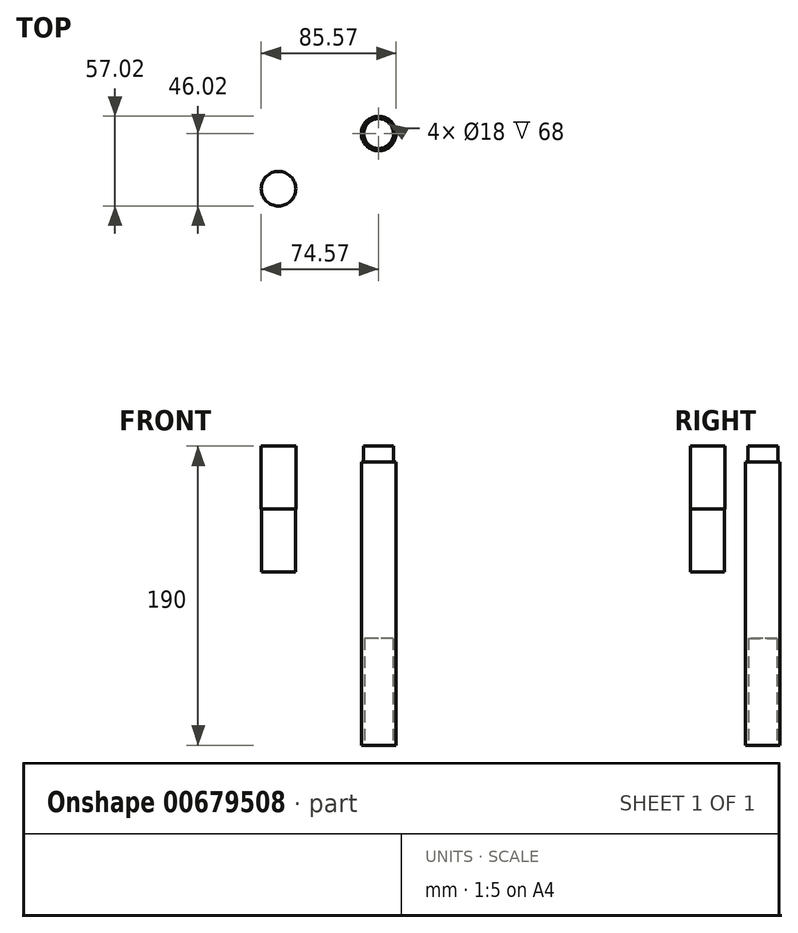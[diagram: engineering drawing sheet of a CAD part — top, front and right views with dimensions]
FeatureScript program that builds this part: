
annotation { "Feature Type Name" : "Feature", "Feature Type Description" : "" }
export const myFeature = defineFeature(function(context is Context, id is Id, definition is map)
    precondition{}
    {
        {
            var Q0;
            Q0=qCreatedBy(makeId("Top.planeOp"),FACE);
            var sketch = newSketch(context, id + "F0", { "sketchPlane" : qUnion([Q0])});
            skCircle(sketch, "E0", {"center": v(0, 0) * mm, "radius": 11 * mm});
            skSolve(sketch);
        }
        {
            var Q0;
            Q0=makeQuery(id+"F0.imprint","IMPRINT",FACE,{"disambiguationData":[TD([[makeQuery(id+"F0.imprint","IMPRINT",EDGE,{"derivedFrom":sQuery(id+"F0.wireOp",EDGE,"E0")}),1.0]])]});
            extrude(context, id + "F1", {"entities" : qUnion([Q0]), "depth" : 180 * mm, "offsetDistance" : 25 * mm});
        }
        {
            var Q0;
            Q0=makeQuery(id+"F1.opExtrude","CAP_FACE",FACE,{"disambiguationData":[OSD([sQuery(id+"F0.wireOp",EDGE,"E0")])],"isStart":false});
            var sketch = newSketch(context, id + "F2", { "sketchPlane" : qUnion([Q0])});
            skCircle(sketch, "E1", {"center": v(0, 0) * mm, "radius": 9.5 * mm});
            skSolve(sketch);
        }
        {
            var Q0;
            Q0=makeQuery(id+"F2.imprint","IMPRINT",FACE,{"disambiguationData":[TD([[makeQuery(id+"F2.imprint","IMPRINT",EDGE,{"derivedFrom":sQuery(id+"F2.wireOp",EDGE,"E1")}),1.0]])]});
            extrude(context, id + "F3", {"entities" : qUnion([Q0]), "operationType" : NewBodyOperationType.ADD, "depth" : 10 * mm, "offsetDistance" : 25 * mm});
        }
        {
            var Q0;
            Q0=makeQuery(id+"F1.opExtrude","CAP_FACE",FACE,{"disambiguationData":[OSD([sQuery(id+"F0.wireOp",EDGE,"E0")])],"isStart":true});
            var sketch = newSketch(context, id + "F4", { "sketchPlane" : qUnion([Q0])});
            skCircle(sketch, "E2", {"center": v(0, 0) * mm, "radius": 9 * mm});
            skSolve(sketch);
        }
        {
            var Q0;
            Q0 = qSketchRegion(id + "F4", true);
            extrude(context, id + "F5", {"entities" : qUnion([Q0]), "operationType" : NewBodyOperationType.REMOVE, "oppositeDirection" : true, "depth" : 68 * mm, "offsetDistance" : 25 * mm});
        }
        {
            var Q0;
            Q0=makeQuery(id+"F1.opExtrude","SWEPT_BODY",BODY,{"disambiguationData":[OSD([sQuery(id+"F0.wireOp",EDGE,"E0")])]});
            var Q1;
            Q1=makeQuery(id+"F1.opExtrude","SWEPT_FACE",FACE,{"disambiguationData":[OSD([sQuery(id+"F0.wireOp",EDGE,"E0")])]});
            circularPattern(context, id + "F6", {"entities" : qUnion([Q0]), "axis" : qUnion([Q1]), "angle" : 360 * degree, "instanceCount" : 4, "equalSpace" : true});
        }
        {
            var Q0;
            Q0=makeQuery(id+"F3.opExtrude","CAP_FACE",FACE,{"disambiguationData":[OSD([sQuery(id+"F2.wireOp",EDGE,"E1")])],"isStart":false});
            var sketch = newSketch(context, id + "F7", { "sketchPlane" : qUnion([Q0])});
            skCircle(sketch, "E3", {"center": v(-63.57, -35.02) * mm, "radius": 11 * mm});
            skSolve(sketch);
        }
        {
            var Q0;
            Q0=makeQuery(id+"F7.imprint","IMPRINT",FACE,{"disambiguationData":[TD([[makeQuery(id+"F7.imprint","IMPRINT",EDGE,{"derivedFrom":sQuery(id+"F7.wireOp",EDGE,"E3")}),1.0]])]});
            extrude(context, id + "F8", {"entities" : qUnion([Q0]), "oppositeDirection" : true, "depth" : 40 * mm, "offsetDistance" : 25 * mm});
        }
        {
            var Q0;
            Q0=makeQuery(id+"F8.opExtrude","CAP_FACE",FACE,{"disambiguationData":[OSD([sQuery(id+"F7.wireOp",EDGE,"E3")])],"isStart":false});
            var sketch = newSketch(context, id + "F9", { "sketchPlane" : qUnion([Q0])});
            skCircle(sketch, "E4", {"center": v(-63.57, 35.02) * mm, "radius": 10.8 * mm});
            skSolve(sketch);
        }
        {
            var Q0;
            Q0 = qSketchRegion(id + "F9", true);
            extrude(context, id + "F10", {"entities" : qUnion([Q0]), "operationType" : NewBodyOperationType.ADD, "depth" : 40 * mm, "offsetDistance" : 25 * mm});
        }
    });
